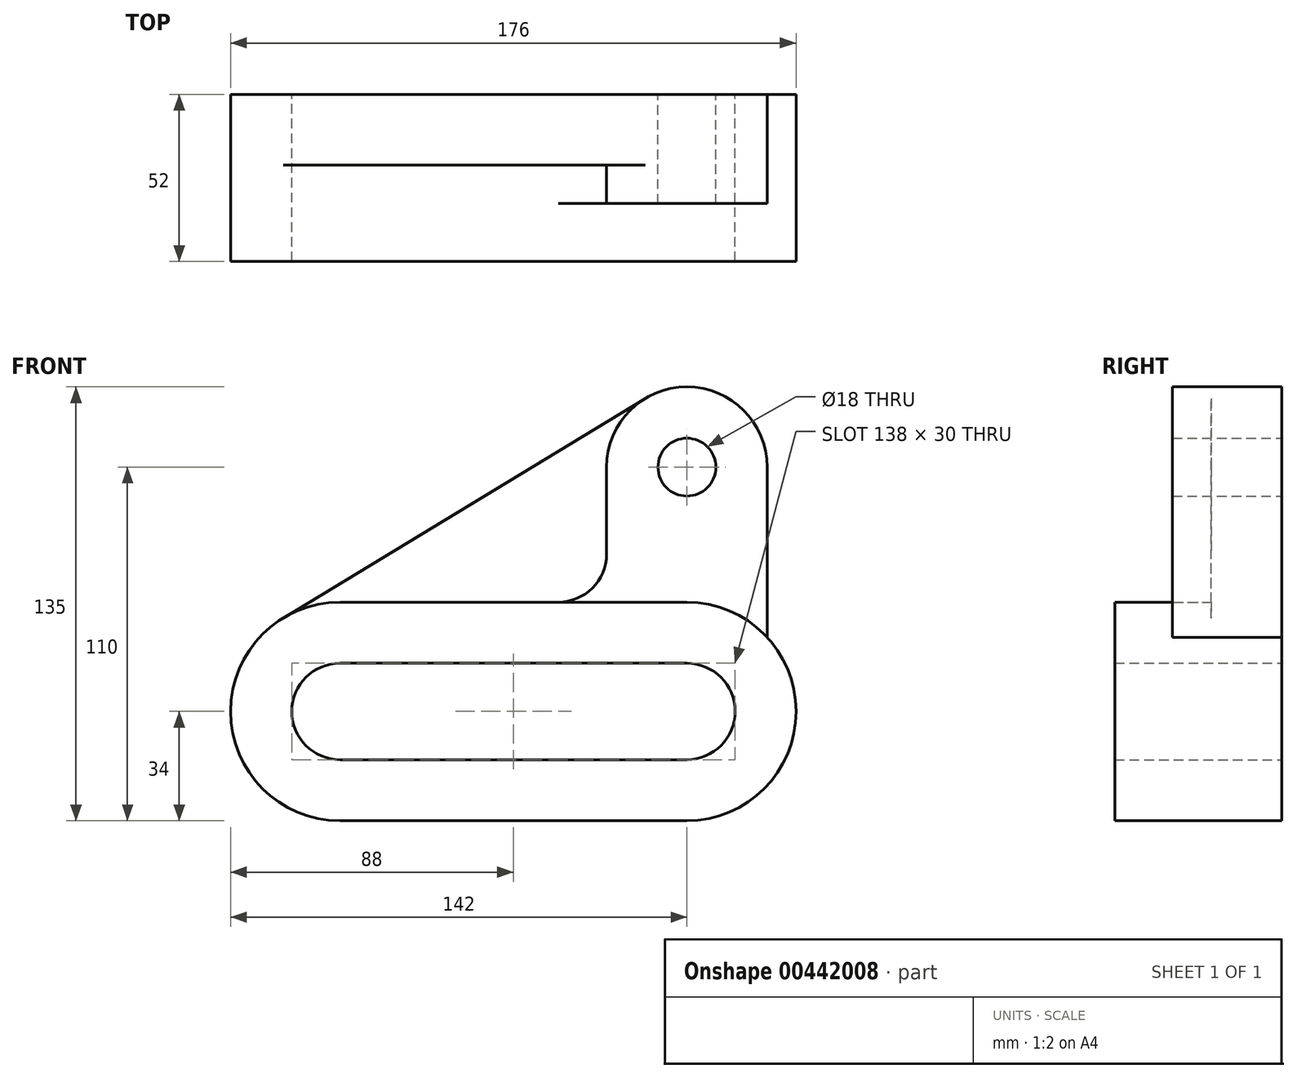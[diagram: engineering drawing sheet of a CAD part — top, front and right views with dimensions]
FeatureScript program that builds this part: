
annotation { "Feature Type Name" : "Feature", "Feature Type Description" : "" }
export const myFeature = defineFeature(function(context is Context, id is Id, definition is map)
    precondition{}
    {
        {
            var Q0;
            Q0=qCreatedBy(makeId("Front.planeOp"),FACE);
            var sketch = newSketch(context, id + "F0", { "sketchPlane" : qUnion([Q0])});
            skPoint(sketch, "E0.middle", {"position": v(0, 0) * mm});
            skArc(sketch, "E1", {"start": v(-54, 34) * mm, "mid": v(-88, 0) * mm, "end": v(-54, -34) * mm});
            skArc(sketch, "E2.trimOffspring", {"start": v(54, -34) * mm, "mid": v(88, 0) * mm, "end": v(54, 34) * mm});
            skLineSegment(sketch, "E3", {"start": v(-54, 34) * mm, "end": v(14, 34) * mm});
            skLineSegment(sketch, "E4", {"start": v(-54, -34) * mm, "end": v(54, -34) * mm});
            skPoint(sketch, "E5.orphan", {"position": v(54, 67) * mm});
            skPoint(sketch, "E6.start.orphan", {"position": v(54, 76) * mm});
            skLineSegment(sketch, "E7", {"start": v(54, 34) * mm, "end": v(27.27, 34) * mm});
            skCircle(sketch, "E8", {"center": v(54, 76) * mm, "radius": 9 * mm});
            skCircle(sketch, "E9", {"center": v(54, 76) * mm, "radius": 25 * mm});
            skLineSegment(sketch, "E10", {"start": v(-71.63, 29.07) * mm, "end": v(41.04, 97.38) * mm});
            skLineSegment(sketch, "E11", {"start": v(29, 76) * mm, "end": v(29, 49) * mm});
            skPoint(sketch, "E12.newPointA", {"position": v(29, 34) * mm});
            skPoint(sketch, "E12.newPointB", {"position": v(27.27, 34) * mm});
            skArc(sketch, "E12.filletArc", {"start": v(14, 34) * mm, "mid": v(24.6, 38.4) * mm, "end": v(29, 49) * mm});
            skLineSegment(sketch, "E13", {"start": v(14, 34) * mm, "end": v(54, 34) * mm});
            skLineSegment(sketch, "E14", {"start": v(79, 76) * mm, "end": v(79, 23.04) * mm});
            skArc(sketch, "E15", {"start": v(-54, 15) * mm, "mid": v(-69, 0) * mm, "end": v(-54, -15) * mm});
            skArc(sketch, "E16", {"start": v(54, -15) * mm, "mid": v(69, 0) * mm, "end": v(54, 15) * mm});
            skLineSegment(sketch, "E17", {"start": v(-54, 15) * mm, "end": v(54, 15) * mm});
            skLineSegment(sketch, "E18", {"start": v(-54, -15) * mm, "end": v(54, -15) * mm});
            skSolve(sketch);
        }
        {
            var Q0;
            {var subQ1=sQuery(id+"F0.wireOp",EDGE,"E3");Q0=makeQuery(id+"F0.imprint","IMPRINT",FACE,{"disambiguationData":[TD([[makeQuery(id+"F0.imprint","IMPRINT",EDGE,{"derivedFrom":subQ1}),-1.0]])]});}
            extrude(context, id + "F1", {"entities" : qUnion([Q0]), "depth" : 52 * mm});
        }
        {
            var Q0;
            {var subQ3=sQuery(id+"F0.wireOp",EDGE,"E3");Q0=makeQuery(id+"F0.imprint","IMPRINT",FACE,{"disambiguationData":[TD([[makeQuery(id+"F0.imprint","IMPRINT",EDGE,{"derivedFrom":subQ3}),1.0]])]});}
            extrude(context, id + "F2", {"entities" : qUnion([Q0]), "operationType" : NewBodyOperationType.ADD, "depth" : 22 * mm});
        }
        {
            var Q0;
            {var subQ1=sQuery(id+"F0.wireOp",EDGE,"E11");Q0=makeQuery(id+"F0.imprint","IMPRINT",FACE,{"disambiguationData":[TD([[makeQuery(id+"F0.imprint","IMPRINT",EDGE,{"derivedFrom":subQ1}),1.0]])]});}
            var Q1;
            Q1=makeQuery(id+"F0.imprint","IMPRINT",FACE,{"disambiguationData":[TD([[makeQuery(id+"F0.imprint","IMPRINT",EDGE,{"derivedFrom":sQuery(id+"F0.wireOp",EDGE,"E8")}),-1.0]])]});
            extrude(context, id + "F3", {"entities" : qUnion([Q0, Q1]), "operationType" : NewBodyOperationType.ADD, "depth" : 34 * mm});
        }
    });
